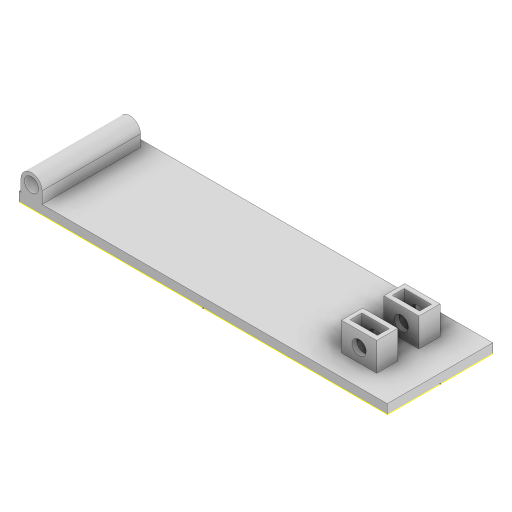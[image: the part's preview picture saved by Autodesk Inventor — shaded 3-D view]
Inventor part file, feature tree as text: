
AUTODESK INVENTOR PART (.ipt)
format: ipt  version: 2023.3 (Build 273359000, 359)  size: 220,672 bytes
history: native  units: mm
features: sketch x6, extrude x5, plane x1, mirror x1, projected_geometry x1
ambient origin geometry x8: Origin, YZ Plane, XZ Plane, XY Plane, X Axis, Y Axis, Z Axis, Center Point
bodies: Solid1 (feature_tree)
feature tree (14):
  extrude  "Extrusion1"  Depth=78.5mm
  extrude  "Extrusion2"  Depth=22.5mm
  extrude  "Extrusion3"  Depth=3.0mm
  extrude  "Extrusion4"  Depth=4.5mm
  plane  "Work Plane1"
  mirror  "Mirror1"
  sketch  "Sketch5"  dims[d9=10.5mm d10=3.0mm]
  extrude  "Extrusion5"  Depth=3.0mm
  sketch  "Sketch1"  dims[d0=2.0mm d1=78.5mm]
  sketch  "Sketch2"  dims[d2=22.5mm d3=0.0mm d4=2.62mm]
  sketch  "Sketch3"  dims[d5=2.5mm d6=3.0mm]
  sketch  "Sketch4"  dims[d7=4.5mm d8=2.875mm]
  projected_geometry  "Projected Loop1"
  sketch  "Sketch6"  dims[d11=4.5mm d12=5.5mm d13=7.5mm d14=0.0mm d15=4.5mm d16=4.5mm d17=4.5mm d18=4.5mm d19=22.5mm d20=0.0mm d21=5.8mm d22=2.5mm d23=5.8mm d24=2.5mm d25=6.351mm d26=0.0mm d27=6.351mm d28=0.0mm d29=2.25mm d30=1.5mm d31=10.0mm d32=0.0mm]
